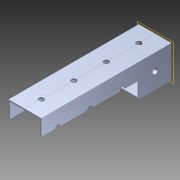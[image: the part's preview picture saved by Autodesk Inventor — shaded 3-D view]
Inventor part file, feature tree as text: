
AUTODESK INVENTOR PART (.ipt)
format: ipt  version: 2014 (Build 180170000, 170)  size: 1,201,664 bytes
history: native  units: in
note: dims shown in document units (in); Inventor stores cm internally (conversion verified against a paired STEP export)
features: extrude x2, sketch x2, pattern_circular x1, other x1, plane x1, imported_body x1
ambient origin geometry x8: Origin, YZ Plane, XZ Plane, XY Plane, X Axis, Y Axis, Z Axis, Center Point
bodies: Body1 (feature_tree)
feature tree (8):
  pattern_circular  "CirPattern2"
  other  "217-3426-STEP1"
  plane  "Work Plane1"
  extrude  "Extrusion1"  Depth=3937.0079in TaperAngle=0.0deg
  extrude  "Extrusion3"  [1 undecoded]
  imported_body  "Base1"
  sketch  "Sketch1"  dims[d0=-4.0in d1=3937.0079in d2=0.0in]
  sketch  "Sketch5"  dims[d5=3.937in d6=0.0in]
note: 1 required parameter value undecoded (feature->parameter linkage not recoverable at this tier; creation-order binding heuristic only, values carry confidence <= 0.55)
